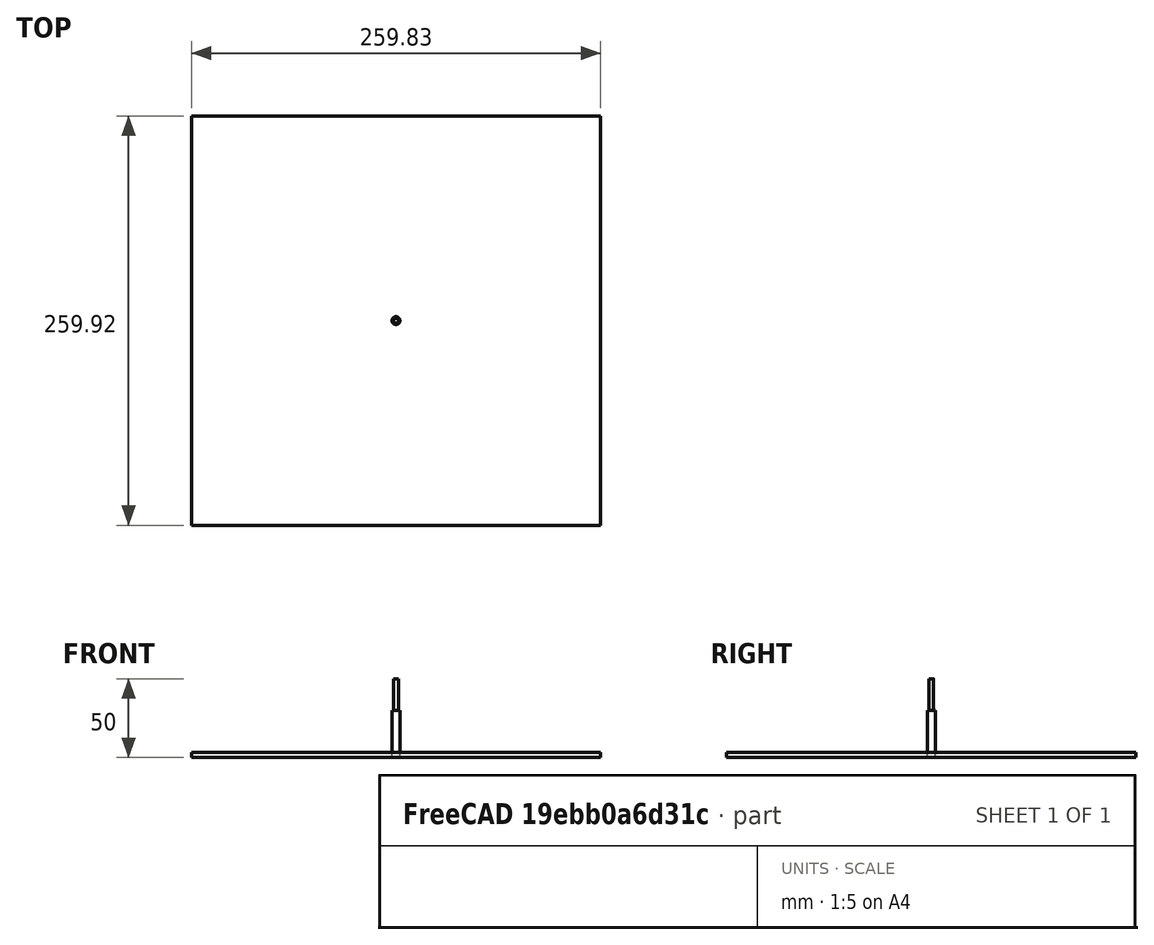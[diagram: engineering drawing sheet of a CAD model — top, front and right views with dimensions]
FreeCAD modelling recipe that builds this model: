
FCSTD DOCUMENT  (FreeCAD 0.19R23777 (Git))
Label: base
License: All rights reserved
LicenseURL: http://en.wikipedia.org/wiki/All_rights_reserved
objects: Path::FeaturePython×5, App::DocumentObjectGroup×2, Part::FeaturePython×2, Sketcher::SketchObject×1, App::FeaturePython×1, Part::Part2DObjectPython×1, Path::FeatureCompoundPython×1, Mesh::FeaturePython×1
note: 6 computed .brp shape members not serialized (recipe doc carries the construction recipe); baked Part::Feature solids carry a one-line shape summary decoded from their .brp

FEATURE [Sketcher::SketchObject] Sketch
  FullyConstrained = false
  sketch-geometry (15):
    g0: Circle CenterX=0 CenterY=0 CenterZ=0 NormalX=0 NormalY=0 NormalZ=1 AngleXU=0 Radius=130
    g1: Circle CenterX=0 CenterY=0 CenterZ=0 NormalX=0 NormalY=0 NormalZ=1 AngleXU=0 Radius=10
    g2: Circle CenterX=13 CenterY=13 CenterZ=0 NormalX=0 NormalY=0 NormalZ=1 AngleXU=0 Radius=2
    g3: Circle CenterX=15.5 CenterY=15.5 CenterZ=0 NormalX=0 NormalY=0 NormalZ=1 AngleXU=0 Radius=2
    g4: Circle CenterX=23.57 CenterY=23.57 CenterZ=0 NormalX=0 NormalY=0 NormalZ=1 AngleXU=0 Radius=2.6
    g5: GeomPoint X=13.6949 Y=14.4226 Z=0
    g6: Circle CenterX=-23.57 CenterY=23.57 CenterZ=0 NormalX=0 NormalY=0 NormalZ=1 AngleXU=0 Radius=2.6
    g7: Circle CenterX=-15.5 CenterY=15.5 CenterZ=0 NormalX=0 NormalY=0 NormalZ=1 AngleXU=0 Radius=2
    g8: Circle CenterX=-13 CenterY=13 CenterZ=0 NormalX=0 NormalY=0 NormalZ=1 AngleXU=0 Radius=2
    g9: Circle CenterX=23.57 CenterY=-23.57 CenterZ=0 NormalX=0 NormalY=0 NormalZ=1 AngleXU=0 Radius=2.6
    g10: Circle CenterX=15.5 CenterY=-15.5 CenterZ=0 NormalX=0 NormalY=0 NormalZ=1 AngleXU=0 Radius=2
    g11: Circle CenterX=13 CenterY=-13 CenterZ=0 NormalX=0 NormalY=0 NormalZ=1 AngleXU=0 Radius=2
    g12: Circle CenterX=-13 CenterY=-13 CenterZ=0 NormalX=0 NormalY=0 NormalZ=1 AngleXU=0 Radius=2
    g13: Circle CenterX=-15.5 CenterY=-15.5 CenterZ=0 NormalX=0 NormalY=0 NormalZ=1 AngleXU=0 Radius=2
    g14: Circle CenterX=-23.57 CenterY=-23.57 CenterZ=0 NormalX=0 NormalY=0 NormalZ=1 AngleXU=0 Radius=2.6
  constraints (22):
    c: Radius(g0) = 130
    c: Coincident(g0,g-1)
    c: Radius(g1) = 10
    c: Coincident(g1,g0)
    c: Radius(g4) = 2.6
    c: Radius(g3) = 2
    c: Radius(g2) = 2
    c: DistanceX(g-1,g2) = 13
    c: DistanceY(g-1,g2) = 13
    c: DistanceX(g3) = 15.5
    c: DistanceY(g-1,g3) = 15.5
    c: DistanceX(g-1,g4) = 23.57
    c: DistanceY(g4) = 23.57
    c: Radius(g6) = 2.6
    c: Radius(g7) = 2
    c: Radius(g8) = 2
    c: Radius(g9) = 2.6
    c: Radius(g10) = 2
    c: Radius(g11) = 2
    c: Radius(g14) = 2.6
    c: Radius(g13) = 2
    c: Radius(g12) = 2
FEATURE [App::FeaturePython] SetupSheet  # Path/CAM operation (typed FeaturePython)
  ClearanceHeightExpression = OpStockZMax+SetupSheet.ClearanceHeightOffset
  ClearanceHeightOffset = 5
  CoolantMode = 0
  CoolantModes = None | Flood | Mist
  FinalDepthExpression = OpFinalDepth
  HorizRapid = 0
  SafeHeightExpression = OpStockZMax+SetupSheet.SafeHeightOffset
  SafeHeightOffset = 3
  StartDepthExpression = OpStartDepth
  StepDownExpression = OpToolDiameter
  VertRapid = 0
FEATURE [Part::Part2DObjectPython] Clone2D  label="Model-Sketch"  # Draft 2D object (typed FeaturePython)
  Fuse = false
  Objects = -> [Sketch]
  PathResource = Model
  Scale = (1,1,1)
FEATURE [App::DocumentObjectGroup] Model
  Group = -> [Clone2D]
FEATURE [Part::FeaturePython] ToolBit  label="Endmill"  # Path/CAM toolbit (typed FeaturePython)
  BitShape = <userpath>/Software/FreeCAD/Mod/Path/Tools/Shape/endmill.fcstd
  CuttingEdgeHeight = 30
  Diameter = 3.125
  Length = 50
  ShankDiameter = 3
  ShapeName = endmill
FEATURE [Path::FeaturePython] TC__Default_Tool  label="TC: Default Tool"  # Path/CAM operation (typed FeaturePython)
  HorizFeed = 5
  HorizRapid = 0
  SpindleDir = 0
  SpindleSpeed = 10000
  Tool = -> ToolBit
  ToolNumber = 1
  VertFeed = 3
  VertRapid = 0
  expr: VertRapid = SetupSheet.VertRapid
  expr: HorizRapid = SetupSheet.HorizRapid
FEATURE [App::DocumentObjectGroup] Tools
  Group = -> [TC__Default_Tool]
FEATURE [Part::FeaturePython] Stock001  # WARN: FeaturePython — macro-defined, semantics opaque (R4)
  Height = 3.2
  Length = 259.83
  Placement = pos=(-129.828,-129.957,0) rot=(0,0,1;0rad)
  StockType = CreateBox
  Width = 259.914
FEATURE [Path::FeaturePython] Profile  # Path/CAM operation (typed FeaturePython)
  Active = true
  AreaParams:
    Tolerance = 1e-07
    FitArcs = True
    Simplify = False
    CleanDistance = 0.0
    Accuracy = 0.01
    Unit = 1.0
    MinArcPoints = 4
    MaxArcPoints = 100
    ClipperScale = 10000000.0
    Fill = 0
    Coplanar = 0
    Reorient = True
    Outline = False
    Explode = False
    OpenMode = 0
    Deflection = 0.01
    SubjectFill = 0
    ClipFill = 0
    Offset = 1.5625
    ExtraPass = 0
    Stepover = 0.0
    LastStepover = 0.0
    JoinType = 0
    EndType = 0
    MiterLimit = 2.0
    RoundPrecision = 0.0
    PocketMode = 0
    ToolRadius = 1.0
    PocketExtraOffset = 0.0
    PocketStepover = 0.0
    PocketLastStepover = 0.0
    FromCenter = False
    Angle = 45.0
    AngleShift = 0.0
    Shift = 0.0
    Thicken = False
    SectionCount = -1
    Stepdown = 1.0
    SectionOffset = 0.0
    SectionTolerance = 1e-06
    SectionMode = 2
    Project = False
  AttemptInverseAngle = true
  ClearanceHeight = 8.2
  CoolantMode = None
  CycleTime = 00:11:35
  Direction = 0
  EnableRotation = 0
  ExpandProfile = 0
  ExpandProfileStepOver = 100
  FinalDepth = 0
  HandleMultipleFeatures = 1
  InverseAngle = false
  JoinType = 0
  LimitDepthToFace = true
  MiterLimit = 0.1
  OffsetExtra = 0
  OpFinalDepth = 0
  OpStartDepth = 3.2
  OpStockZMax = 3.2
  OpStockZMin = 0
  OpToolDiameter = 3.125
  PathParams = {'orientation': 1, 'feedrate': 5.0, 'feedrate_v': 3.0, 'verbose': True, 'resume_height': 6.2, 'retraction': 8.2, 'return_end': True, 'preamble': False}
  ReverseDirection = false
  SafeHeight = 6.2
  Side = 0
  StartDepth = 3.2
  StartPoint = (0,0,0)
  StepDown = 1
  ToolController = -> TC__Default_Tool
  UseComp = true
  UseStartPoint = false
  processCircles = false
  processHoles = false
  processPerimeter = true
  expr: StartDepth = OpStartDepth
  expr: FinalDepth = OpFinalDepth
  expr: StepDown = 1
  expr: SafeHeight = OpStockZMax + SetupSheet.SafeHeightOffset
  expr: ClearanceHeight = OpStockZMax + SetupSheet.ClearanceHeightOffset
FEATURE [Path::FeaturePython] Profile001  # Path/CAM operation (typed FeaturePython)
  Active = true
  AreaParams:
    Tolerance = 1e-07
    FitArcs = True
    Simplify = False
    CleanDistance = 0.0
    Accuracy = 0.01
    Unit = 1.0
    MinArcPoints = 4
    MaxArcPoints = 100
    ClipperScale = 10000000.0
    Fill = 0
    Coplanar = 0
    Reorient = True
    Outline = False
    Explode = False
    OpenMode = 0
    Deflection = 0.01
    SubjectFill = 0
    ClipFill = 0
    Offset = -1.5625
    ExtraPass = 0
    Stepover = 0.0
    LastStepover = 0.0
    JoinType = 0
    EndType = 0
    MiterLimit = 2.0
    RoundPrecision = 0.0
    PocketMode = 0
    ToolRadius = 1.0
    PocketExtraOffset = 0.0
    PocketStepover = 0.0
    PocketLastStepover = 0.0
    FromCenter = False
    Angle = 45.0
    AngleShift = 0.0
    Shift = 0.0
    Thicken = False
    SectionCount = -1
    Stepdown = 1.0
    SectionOffset = 0.0
    SectionTolerance = 1e-06
    SectionMode = 2
    Project = False
  AttemptInverseAngle = true
  Base = -> [Clone2D]
  ClearanceHeight = 8.2
  CoolantMode = None
  CycleTime = 00:00:51
  Direction = 0
  EnableRotation = 0
  ExpandProfile = 0
  ExpandProfileStepOver = 100
  FinalDepth = 0
  HandleMultipleFeatures = 1
  InverseAngle = false
  JoinType = 0
  LimitDepthToFace = true
  MiterLimit = 0.1
  OffsetExtra = 0
  OpFinalDepth = 0
  OpStartDepth = 3.2
  OpStockZMax = 3.2
  OpStockZMin = 0
  OpToolDiameter = 3.125
  PathParams = {'orientation': 1, 'feedrate': 5.0, 'feedrate_v': 3.0, 'verbose': True, 'resume_height': 6.2, 'retraction': 8.2, 'return_end': True, 'preamble': False}
  ReverseDirection = false
  SafeHeight = 6.2
  Side = 1
  StartDepth = 3.2
  StartPoint = (0,0,0)
  StepDown = 1
  ToolController = -> TC__Default_Tool
  UseComp = true
  UseStartPoint = false
  processCircles = false
  processHoles = false
  processPerimeter = true
  expr: StartDepth = OpStartDepth
  expr: FinalDepth = OpFinalDepth
  expr: StepDown = 1
  expr: SafeHeight = OpStockZMax + SetupSheet.SafeHeightOffset
  expr: ClearanceHeight = OpStockZMax + SetupSheet.ClearanceHeightOffset
FEATURE [Path::FeaturePython] Helix  # Path/CAM operation (typed FeaturePython)
  Active = true
  Base = -> [Clone2D]
  ClearanceHeight = 8.2
  CoolantMode = None
  CycleTime = 00:01:43
  Direction = 0
  Disabled = Clone2D.Edge1 | Clone2D.Edge2
  EnableRotation = 0
  FinalDepth = 0
  OpFinalDepth = 0
  OpStartDepth = 3.2
  OpStockZMax = 3.2
  OpStockZMin = 0
  OpToolDiameter = 3.125
  SafeHeight = 6.2
  StartDepth = 3.2
  StartRadius = 0
  StartSide = 0
  StepDown = 3.125
  StepOver = 100
  ToolController = -> TC__Default_Tool
  expr: ClearanceHeight = OpStockZMax + SetupSheet.ClearanceHeightOffset
  expr: SafeHeight = OpStockZMax + SetupSheet.SafeHeightOffset
  expr: StepDown = OpToolDiameter
  expr: FinalDepth = OpFinalDepth
  expr: StartDepth = OpStartDepth
FEATURE [Path::FeatureCompoundPython] Operations  # Path/CAM operation (typed FeaturePython)
  Group = -> [Helix,Profile001,Profile]
  UsePlacements = false
FEATURE [Path::FeaturePython] Job  # Path/CAM operation (typed FeaturePython)
  CycleTime = 00:14:09
  Fixtures = G54
  GeometryTolerance = 0.01
  LastPostProcessDate = 2021-02-02 13:21:50.852108
  LastPostProcessOutput = <userpath>/Ultimachine/foc-fixture/dial_260mm/base.nc
  Model = -> Model
  Operations = -> Operations
  OrderOutputBy = 0
  PostProcessor = 7
  PostProcessorOutputFile = <userpath>/Ultimachine/foc-fixture/dial_260mm/base.nc
  SetupSheet = -> SetupSheet
  SplitOutput = false
  Stock = -> Stock001
  Tools = -> Tools
FEATURE [Mesh::FeaturePython] CutMaterial  # WARN: FeaturePython — macro-defined, semantics opaque (R4)
